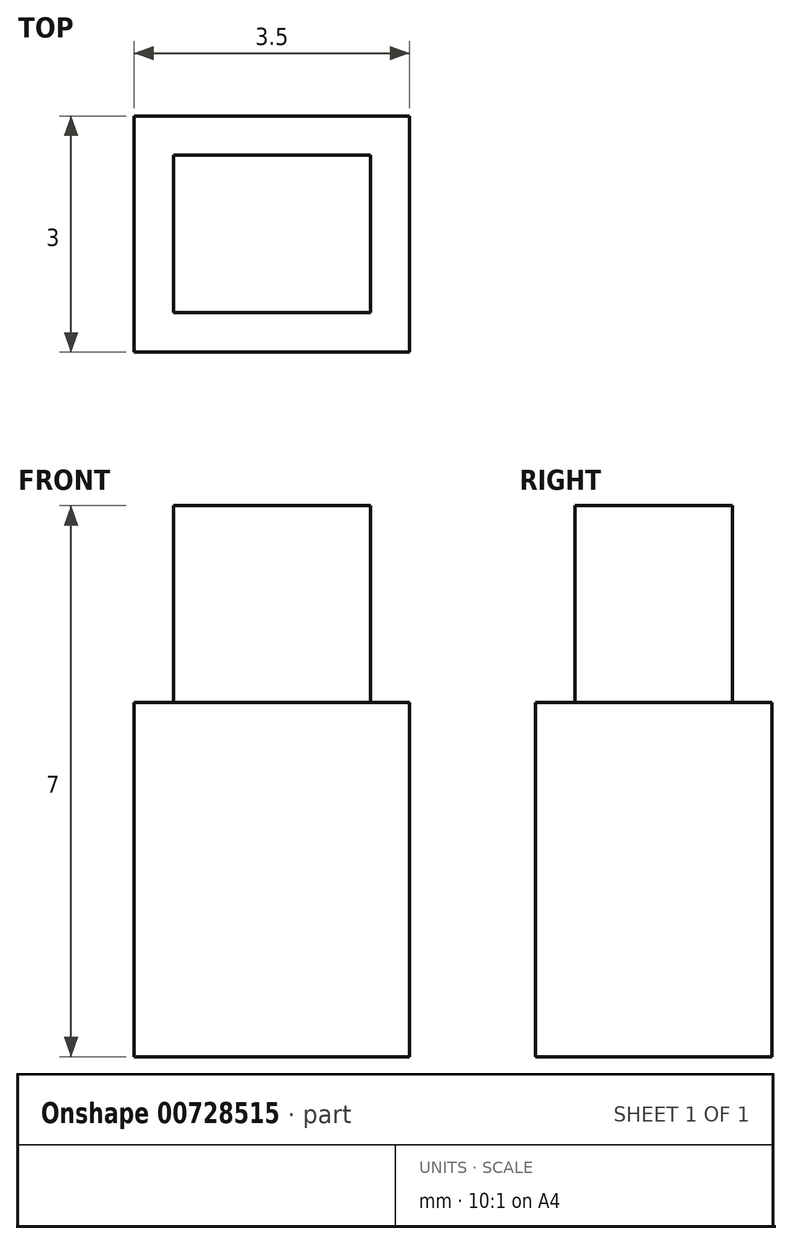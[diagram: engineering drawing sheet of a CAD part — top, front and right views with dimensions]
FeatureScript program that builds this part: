
annotation { "Feature Type Name" : "Feature", "Feature Type Description" : "" }
export const myFeature = defineFeature(function(context is Context, id is Id, definition is map)
    precondition{}
    {
        {
            var Q0;
            Q0=qCreatedBy(makeId("Top.planeOp"),FACE);
            var sketch = newSketch(context, id + "F0", { "sketchPlane" : qUnion([Q0])});
            skLineSegment(sketch, "E0.bottom", {"start": v(-1.75, 1.5) * mm, "end": v(1.75, 1.5) * mm});
            skLineSegment(sketch, "E0.top", {"start": v(-1.75, -1.5) * mm, "end": v(1.75, -1.5) * mm});
            skLineSegment(sketch, "E0.left", {"start": v(-1.75, 1.5) * mm, "end": v(-1.75, -1.5) * mm});
            skLineSegment(sketch, "E0.right", {"start": v(1.75, 1.5) * mm, "end": v(1.75, -1.5) * mm});
            skLineSegment(sketch, "E1", {"start": v(0, -2.85) * mm, "end": v(0, 2.85) * mm, "construction": true});
            skLineSegment(sketch, "E2", {"start": v(-2.85, 0) * mm, "end": v(2.85, 0) * mm, "construction": true});
            skSolve(sketch);
        }
        {
            var Q0;
            Q0=makeQuery(id+"F0.imprint","IMPRINT",FACE,{"disambiguationData":[TD([[makeQuery(id+"F0.imprint","IMPRINT",EDGE,{"derivedFrom":sQuery(id+"F0.wireOp",EDGE,"E0.bottom")}),-1.0]])]});
            extrude(context, id + "F1", {"entities" : qUnion([Q0]), "depth" : (7 - 2.5) * mm, "offsetDistance" : 25 * mm});
        }
        {
            var Q0;
            Q0=makeQuery(id+"F0.imprint","IMPRINT",FACE,{"disambiguationData":[TD([[makeQuery(id+"F0.imprint","IMPRINT",EDGE,{"derivedFrom":sQuery(id+"F0.wireOp",EDGE,"E0.bottom")}),-1.0]])]});
            var sketch = newSketch(context, id + "F2", { "sketchPlane" : qUnion([Q0])});
            skLineSegment(sketch, "E3.0", {"start": v(-1.25, 1) * mm, "end": v(-1.25, -1) * mm});
            skLineSegment(sketch, "E3.1", {"start": v(1.25, 1) * mm, "end": v(-1.25, 1) * mm});
            skLineSegment(sketch, "E3.2", {"start": v(1.25, -1) * mm, "end": v(1.25, 1) * mm});
            skLineSegment(sketch, "E3.3", {"start": v(-1.25, -1) * mm, "end": v(1.25, -1) * mm});
            skSolve(sketch);
        }
        {
            var Q0;
            Q0=makeQuery(id+"F2.imprint","IMPRINT",FACE,{"disambiguationData":[TD([[makeQuery(id+"F2.imprint","IMPRINT",EDGE,{"derivedFrom":sQuery(id+"F2.wireOp",EDGE,"E3.0")}),1.0]])]});
            extrude(context, id + "F3", {"entities" : qUnion([Q0]), "operationType" : NewBodyOperationType.ADD, "depth" : 7 * mm, "offsetDistance" : 25 * mm});
        }
    });
